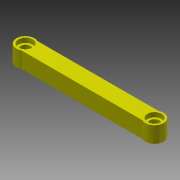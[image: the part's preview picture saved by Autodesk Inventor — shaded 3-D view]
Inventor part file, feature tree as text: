
AUTODESK INVENTOR PART (.ipt)
format: ipt  version: 2013 (Build 170138000, 138)  size: 102,912 bytes
history: native  units: mm
features: extrude x4, sketch x4, chamfer x1, projected_geometry x1
ambient origin geometry x8: Origin, YZ Plane, XZ Plane, XY Plane, X Axis, Y Axis, Z Axis, Center Point
bodies: Solid1 (feature_tree)
feature tree (10):
  extrude  "Extrusion1"  Depth=14.0mm
  extrude  "Extrusion2"  Depth=25.0mm TaperAngle=0.0deg
  extrude  "Extrusion3"  Depth=7.0mm TaperAngle=0.0deg
  extrude  "Extrusion4"  Depth=15.1mm
  chamfer  "Chamfer1"  Distance=7.0mm
  sketch  "Sketch1"  dims[d0=25.0mm d2=14.0mm]
  sketch  "Sketch2"  dims[d3=200.0mm d4=25.0mm d5=0.0mm]
  sketch  "Sketch3"  dims[d6=22.1mm d8=7.0mm d9=0.0mm]
  sketch  "Sketch4"  dims[d10=7.0mm d11=0.0mm d12=15.1mm d14=7.0mm d15=0.0mm d17=3.5mm d18=2.0mm d19=45.0deg]
  projected_geometry  "Projected Loop1"
